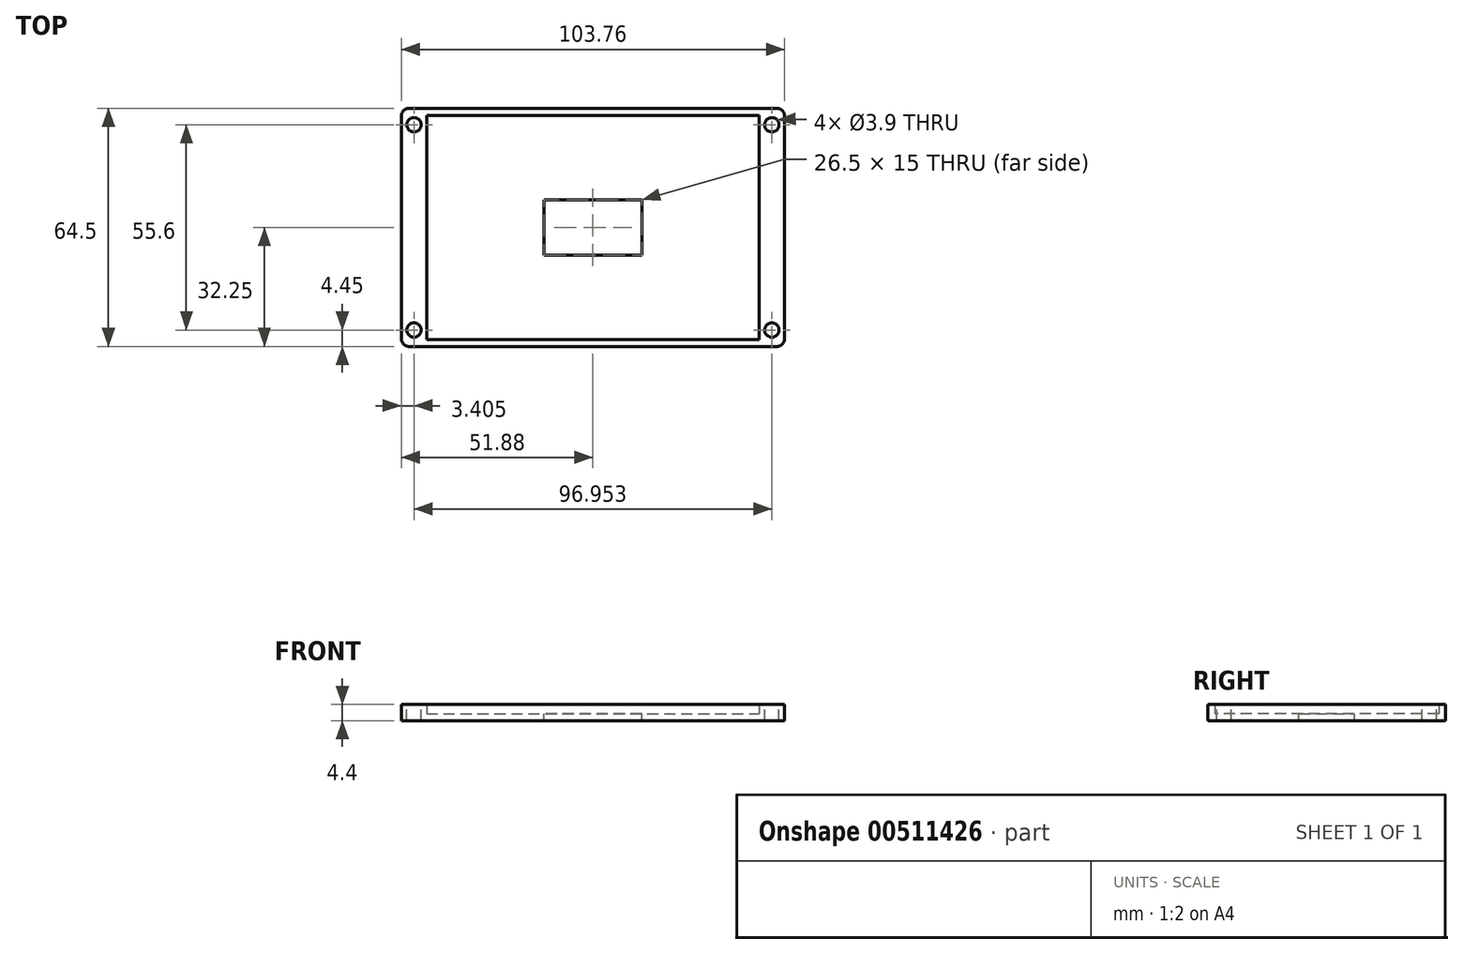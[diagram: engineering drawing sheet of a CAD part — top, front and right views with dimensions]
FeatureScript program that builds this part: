
annotation { "Feature Type Name" : "Feature", "Feature Type Description" : "" }
export const myFeature = defineFeature(function(context is Context, id is Id, definition is map)
    precondition{}
    {
        {
            var Q0;
            Q0=qCreatedBy(makeId("Top.planeOp"),FACE);
            var sketch = newSketch(context, id + "F0", { "sketchPlane" : qUnion([Q0])});
            skLineSegment(sketch, "E0.bottom", {"start": v(-51.88, 32.25) * mm, "end": v(51.88, 32.25) * mm});
            skLineSegment(sketch, "E0.top", {"start": v(-51.88, -32.25) * mm, "end": v(51.88, -32.25) * mm});
            skLineSegment(sketch, "E0.left", {"start": v(-51.88, 32.25) * mm, "end": v(-51.88, -32.25) * mm});
            skLineSegment(sketch, "E0.right", {"start": v(51.88, 32.25) * mm, "end": v(51.88, -32.25) * mm});
            skPoint(sketch, "E0.middle", {"position": v(0, 0) * mm});
            skSolve(sketch);
        }
        {
            var Q0;
            Q0=makeQuery(id+"F0.imprint","IMPRINT",FACE,{"disambiguationData":[TD([[makeQuery(id+"F0.imprint","IMPRINT",EDGE,{"derivedFrom":sQuery(id+"F0.wireOp",EDGE,"E0.bottom")}),-1.0]])]});
            extrude(context, id + "F1", {"entities" : qUnion([Q0]), "endBound" : BoundingType.SYMMETRIC, "depth" : 4.4 * mm});
        }
        {
            var Q0;
            Q0=makeQuery(id+"F1.opExtrude","CAP_FACE",FACE,{"disambiguationData":[OSD([sQuery(id+"F0.wireOp",EDGE,"E0.bottom"),sQuery(id+"F0.wireOp",EDGE,"E0.top"),sQuery(id+"F0.wireOp",EDGE,"E0.left"),sQuery(id+"F0.wireOp",EDGE,"E0.right")])],"isStart":false});
            shell(context, id + "F2", {"entities" : qUnion([Q0]), "thickness" : 1.9 * mm});
        }
        {
            var Q0;
            Q0=qCreatedBy(makeId("Top.planeOp"),FACE);
            var sketch = newSketch(context, id + "F3", { "sketchPlane" : qUnion([Q0])});
            skLineSegment(sketch, "E1.bottom", {"start": v(13.25, -7.5) * mm, "end": v(-13.25, -7.5) * mm});
            skLineSegment(sketch, "E1.top", {"start": v(13.25, 7.5) * mm, "end": v(-13.25, 7.5) * mm});
            skLineSegment(sketch, "E1.left", {"start": v(13.25, -7.5) * mm, "end": v(13.25, 7.5) * mm});
            skLineSegment(sketch, "E1.right", {"start": v(-13.25, -7.5) * mm, "end": v(-13.25, 7.5) * mm});
            skPoint(sketch, "E1.middle", {"position": v(0, 0) * mm});
            skSolve(sketch);
        }
        {
            var Q0;
            Q0=qSketchRegion(id+"F3",true);
            extrude(context, id + "F4", {"entities" : qUnion([Q0]), "operationType" : NewBodyOperationType.REMOVE, "endBound" : BoundingType.SYMMETRIC, "oppositeDirection" : true, "depth" : 25.4 * mm});
        }
        {
            var Q0;
            Q0=makeQuery(id+"F1.opExtrude","SWEPT_EDGE",EDGE,{"disambiguationData":[OSD([sQuery(id+"F0.wireOp",EDGE,"E0.bottom"),sQuery(id+"F0.wireOp",EDGE,"E0.left")])]});
            fillet(context, id + "F5", {"entities" : qUnion([Q0]), "radius" : 2 * mm, "tangentPropagation" : true, "allowEdgeOverflow" : false});
        }
        {
            var Q0;
            Q0=makeQuery(id+"F1.opExtrude","SWEPT_EDGE",EDGE,{"disambiguationData":[OSD([sQuery(id+"F0.wireOp",EDGE,"E0.top"),sQuery(id+"F0.wireOp",EDGE,"E0.left")])]});
            var Q1;
            Q1=makeQuery(id+"F1.opExtrude","SWEPT_EDGE",EDGE,{"disambiguationData":[OSD([sQuery(id+"F0.wireOp",EDGE,"E0.top"),sQuery(id+"F0.wireOp",EDGE,"E0.right")])]});
            var Q2;
            Q2=makeQuery(id+"F1.opExtrude","SWEPT_EDGE",EDGE,{"disambiguationData":[OSD([sQuery(id+"F0.wireOp",EDGE,"E0.bottom"),sQuery(id+"F0.wireOp",EDGE,"E0.right")])]});
            fillet(context, id + "F6", {"entities" : qUnion([Q0, Q1, Q2]), "radius" : 2 * mm, "tangentPropagation" : true, "allowEdgeOverflow" : false});
        }
        {
            var Q0;
            Q0=makeQuery(id+"F2.opShell","OFFSET_FACE",FACE,{"disambiguationData":[OSD([sQuery(id+"F0.wireOp",EDGE,"E0.bottom"),sQuery(id+"F0.wireOp",EDGE,"E0.top"),sQuery(id+"F0.wireOp",EDGE,"E0.left"),sQuery(id+"F0.wireOp",EDGE,"E0.right")])]});
            var sketch = newSketch(context, id + "F7", { "sketchPlane" : qUnion([Q0])});
            skLineSegment(sketch, "E2.bottom", {"start": v(-49.98, -30.35) * mm, "end": v(-45.08, -30.35) * mm});
            skLineSegment(sketch, "E2.top", {"start": v(-49.98, 30.35) * mm, "end": v(-45.08, 30.35) * mm});
            skLineSegment(sketch, "E2.left", {"start": v(-49.98, -30.35) * mm, "end": v(-49.98, 30.35) * mm});
            skLineSegment(sketch, "E2.right", {"start": v(-45.08, -30.35) * mm, "end": v(-45.08, 30.35) * mm});
            skSolve(sketch);
        }
        {
            var Q0;
            Q0=qSketchRegion(id+"F7",true);
            extrude(context, id + "F8", {"entities" : qUnion([Q0]), "operationType" : NewBodyOperationType.ADD, "depth" : 2.5 * mm});
        }
        {
            var Q0;
            Q0=makeQuery(id+"F2.opShell","OFFSET_FACE",FACE,{"disambiguationData":[OSD([sQuery(id+"F0.wireOp",EDGE,"E0.bottom"),sQuery(id+"F0.wireOp",EDGE,"E0.top"),sQuery(id+"F0.wireOp",EDGE,"E0.left"),sQuery(id+"F0.wireOp",EDGE,"E0.right")])]});
            var sketch = newSketch(context, id + "F9", { "sketchPlane" : qUnion([Q0])});
            skLineSegment(sketch, "E3.bottom", {"start": v(49.98, 30.35) * mm, "end": v(45.08, 30.35) * mm});
            skLineSegment(sketch, "E3.top", {"start": v(49.98, -30.35) * mm, "end": v(45.08, -30.35) * mm});
            skLineSegment(sketch, "E3.left", {"start": v(49.98, 30.35) * mm, "end": v(49.98, -30.35) * mm});
            skLineSegment(sketch, "E3.right", {"start": v(45.08, 30.35) * mm, "end": v(45.08, -30.35) * mm});
            skSolve(sketch);
        }
        {
            var Q0;
            Q0=qSketchRegion(id+"F9",true);
            extrude(context, id + "F10", {"entities" : qUnion([Q0]), "operationType" : NewBodyOperationType.ADD, "depth" : 2.5 * mm});
        }
        {
            var Q0;
            Q0=makeQuery(id+"F10.boolean.opBoolean","MERGE",FACE,{"derivedFrom":[makeQuery(id+"F8.boolean.opBoolean","MERGE",FACE,{"derivedFrom":[makeQuery(id+"F1.opExtrude","CAP_FACE",FACE,{"disambiguationData":[OSD([sQuery(id+"F0.wireOp",EDGE,"E0.bottom"),sQuery(id+"F0.wireOp",EDGE,"E0.top"),sQuery(id+"F0.wireOp",EDGE,"E0.left"),sQuery(id+"F0.wireOp",EDGE,"E0.right")])],"isStart":false}),makeQuery(id+"F8.opExtrude","CAP_FACE",FACE,{"disambiguationData":[OSD([sQuery(id+"F7.wireOp",EDGE,"E2.bottom"),sQuery(id+"F7.wireOp",EDGE,"E2.top"),sQuery(id+"F7.wireOp",EDGE,"E2.left"),sQuery(id+"F7.wireOp",EDGE,"E2.right")])],"isStart":false})]}),makeQuery(id+"F10.opExtrude","CAP_FACE",FACE,{"disambiguationData":[OSD([sQuery(id+"F9.wireOp",EDGE,"E3.bottom"),sQuery(id+"F9.wireOp",EDGE,"E3.top"),sQuery(id+"F9.wireOp",EDGE,"E3.left"),sQuery(id+"F9.wireOp",EDGE,"E3.right")])],"isStart":false})]});
            var sketch = newSketch(context, id + "F11", { "sketchPlane" : qUnion([Q0])});
            skCircle(sketch, "E4", {"center": v(-48.48, 27.8) * mm, "radius": 1.95 * mm});
            skPoint(sketch, "E4.centerSnap0", {"position": v(-48.48, 31.25) * mm});
            skPoint(sketch, "E4.centerSnap1", {"position": v(-51.88, 27.8) * mm});
            skCircle(sketch, "E5", {"center": v(48.47, 27.8) * mm, "radius": 1.95 * mm});
            skCircle(sketch, "E6", {"center": v(-48.47, -27.8) * mm, "radius": 1.95 * mm});
            skPoint(sketch, "E6.centerSnap0", {"position": v(-48.47, -23.55) * mm});
            skPoint(sketch, "E6.centerSnap1", {"position": v(-51.87, -27.8) * mm});
            skCircle(sketch, "E7", {"center": v(48.48, -27.8) * mm, "radius": 1.95 * mm});
            skLineSegment(sketch, "E8", {"start": v(-48.48, 32.25) * mm, "end": v(-48.48, 29.75) * mm});
            skLineSegment(sketch, "E9", {"start": v(48.47, 32.25) * mm, "end": v(48.47, 29.75) * mm});
            skLineSegment(sketch, "E10", {"start": v(48.48, -32.25) * mm, "end": v(48.48, -29.75) * mm});
            skLineSegment(sketch, "E11", {"start": v(-48.47, -32.25) * mm, "end": v(-48.47, -29.75) * mm});
            skSolve(sketch);
        }
        {
            var Q0;
            Q0 = qSketchRegion(id + "F11", true);
            extrude(context, id + "F12", {"entities" : qUnion([Q0]), "operationType" : NewBodyOperationType.REMOVE, "oppositeDirection" : true, "depth" : 4.4 * mm, "offsetDistance" : 25.4 * mm});
        }
    });
